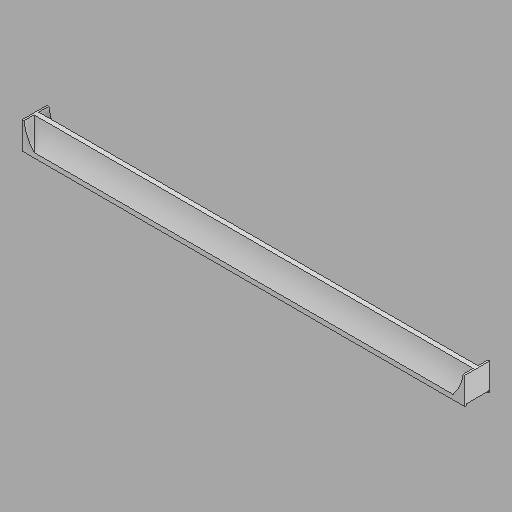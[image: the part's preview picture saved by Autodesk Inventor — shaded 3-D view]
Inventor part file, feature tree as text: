
AUTODESK INVENTOR PART (.ipt)
format: ipt  version: 2022.2 (Build 262287010, 287A)  size: 131,072 bytes
history: native  units: in
note: dims shown in document units (in); Inventor stores cm internally (conversion verified against a paired STEP export)
features: direct_edit x1, other x1, revolve x1
ambient origin geometry x8: Origin, YZ Plane, XZ Plane, XY Plane, X Axis, Y Axis, Z Axis, Center Point
bodies: Solid1 (feature_tree)
feature tree (3):
  direct_edit  "Direct Edit1"
  other  "Transom (Center)"
  revolve  "Rotate1"  [1 undecoded]
note: 1 required parameter value undecoded (feature->parameter linkage not recoverable at this tier; creation-order binding heuristic only, values carry confidence <= 0.55)
